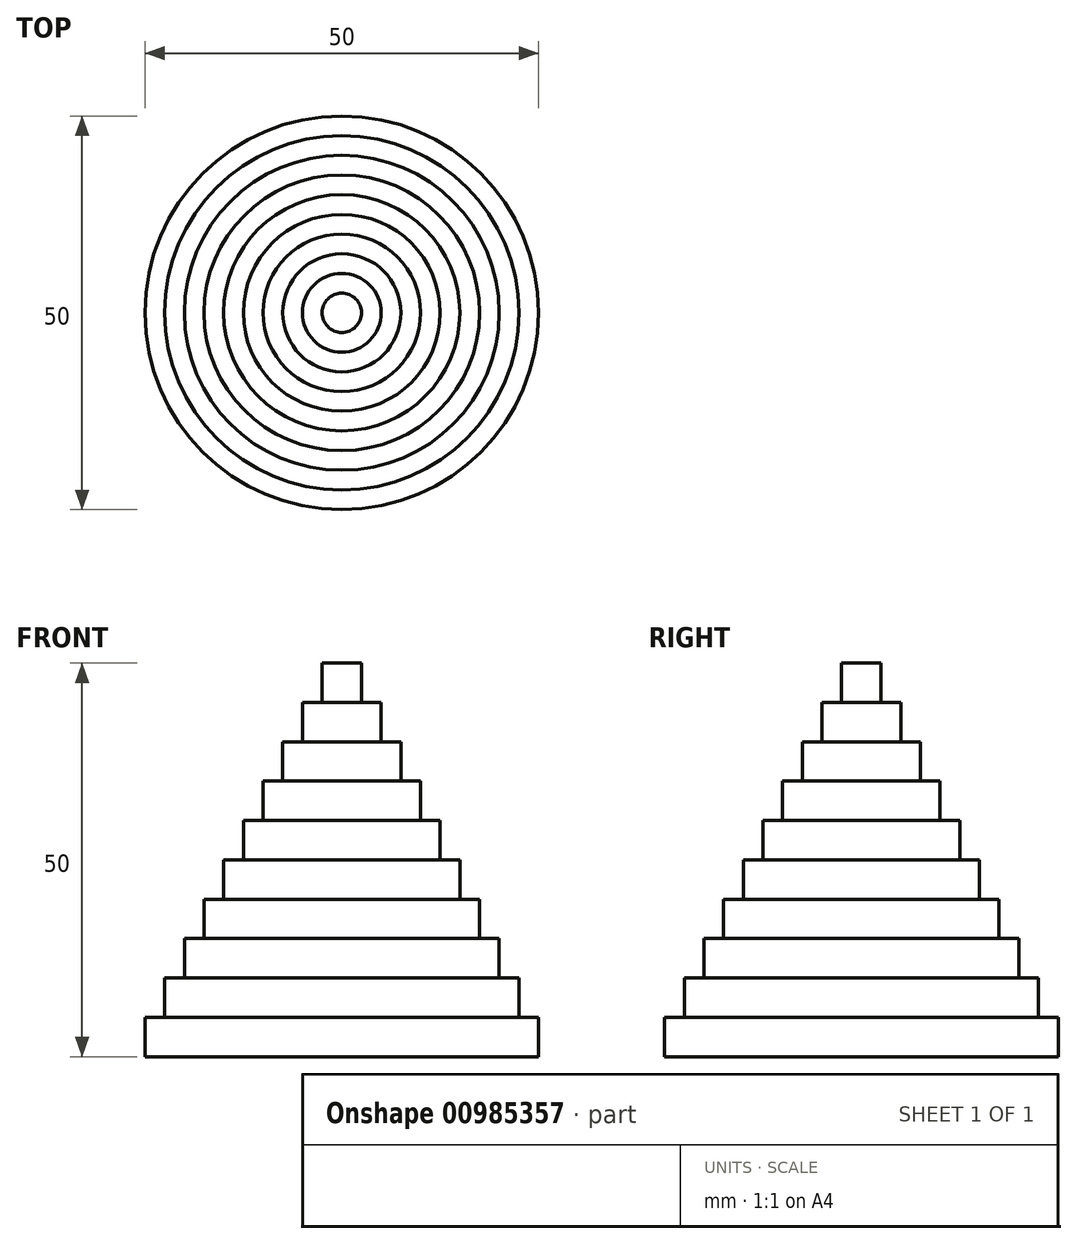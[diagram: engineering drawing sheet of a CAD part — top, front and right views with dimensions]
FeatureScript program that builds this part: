
annotation { "Feature Type Name" : "Feature", "Feature Type Description" : "" }
export const myFeature = defineFeature(function(context is Context, id is Id, definition is map)
    precondition{}
    {
        {
            var Q0;
            Q0=qCreatedBy(makeId("Top.planeOp"),FACE);
            var sketch = newSketch(context, id + "F0", { "sketchPlane" : qUnion([Q0])});
            skCircle(sketch, "E0", {"center": v(0, 0) * mm, "radius": 2.5 * mm});
            skCircle(sketch, "E1", {"center": v(0, 0) * mm, "radius": 5 * mm});
            skCircle(sketch, "E2", {"center": v(0, 0) * mm, "radius": 7.5 * mm});
            skCircle(sketch, "E3", {"center": v(0, 0) * mm, "radius": 10 * mm});
            skCircle(sketch, "E4", {"center": v(0, 0) * mm, "radius": 12.5 * mm});
            skCircle(sketch, "E5", {"center": v(0, 0) * mm, "radius": 15 * mm});
            skCircle(sketch, "E6", {"center": v(0, 0) * mm, "radius": 17.5 * mm});
            skCircle(sketch, "E7", {"center": v(0, 0) * mm, "radius": 20 * mm});
            skCircle(sketch, "E8", {"center": v(0, 0) * mm, "radius": 22.5 * mm});
            skCircle(sketch, "E9", {"center": v(0, 0) * mm, "radius": 25 * mm});
            skSolve(sketch);
        }
        {
            var Q0;
            Q0=makeQuery(id+"F0.imprint","IMPRINT",FACE,{"disambiguationData":[TD([[makeQuery(id+"F0.imprint","IMPRINT",EDGE,{"derivedFrom":sQuery(id+"F0.wireOp",EDGE,"E5")}),-1.0]])]});
            var Q1;
            Q1=makeQuery(id+"F0.imprint","IMPRINT",FACE,{"disambiguationData":[TD([[makeQuery(id+"F0.imprint","IMPRINT",EDGE,{"derivedFrom":sQuery(id+"F0.wireOp",EDGE,"E3")}),-1.0]])]});
            var Q2;
            Q2=makeQuery(id+"F0.imprint","IMPRINT",FACE,{"disambiguationData":[TD([[makeQuery(id+"F0.imprint","IMPRINT",EDGE,{"derivedFrom":sQuery(id+"F0.wireOp",EDGE,"E1")}),-1.0]])]});
            var Q3;
            Q3=makeQuery(id+"F0.imprint","IMPRINT",FACE,{"disambiguationData":[TD([[makeQuery(id+"F0.imprint","IMPRINT",EDGE,{"derivedFrom":sQuery(id+"F0.wireOp",EDGE,"E2")}),-1.0]])]});
            var Q4;
            Q4=makeQuery(id+"F0.imprint","IMPRINT",FACE,{"disambiguationData":[TD([[makeQuery(id+"F0.imprint","IMPRINT",EDGE,{"derivedFrom":sQuery(id+"F0.wireOp",EDGE,"E6")}),-1.0]])]});
            var Q5;
            Q5=makeQuery(id+"F0.imprint","IMPRINT",FACE,{"disambiguationData":[TD([[makeQuery(id+"F0.imprint","IMPRINT",EDGE,{"derivedFrom":sQuery(id+"F0.wireOp",EDGE,"E4")}),-1.0]])]});
            var Q6;
            Q6=makeQuery(id+"F0.imprint","IMPRINT",FACE,{"disambiguationData":[TD([[makeQuery(id+"F0.imprint","IMPRINT",EDGE,{"derivedFrom":sQuery(id+"F0.wireOp",EDGE,"E8")}),-1.0]])]});
            var Q7;
            Q7=makeQuery(id+"F0.imprint","IMPRINT",FACE,{"disambiguationData":[TD([[makeQuery(id+"F0.imprint","IMPRINT",EDGE,{"derivedFrom":sQuery(id+"F0.wireOp",EDGE,"E0")}),1.0]])]});
            var Q8;
            Q8=makeQuery(id+"F0.imprint","IMPRINT",FACE,{"disambiguationData":[TD([[makeQuery(id+"F0.imprint","IMPRINT",EDGE,{"derivedFrom":sQuery(id+"F0.wireOp",EDGE,"E7")}),-1.0]])]});
            var Q9;
            Q9=makeQuery(id+"F0.imprint","IMPRINT",FACE,{"disambiguationData":[TD([[makeQuery(id+"F0.imprint","IMPRINT",EDGE,{"derivedFrom":sQuery(id+"F0.wireOp",EDGE,"E0")}),-1.0]])]});
            extrude(context, id + "F1", {"entities" : qUnion([Q0, Q1, Q2, Q3, Q4, Q5, Q6, Q7, Q8, Q9]), "depth" : 5 * mm, "offsetDistance" : 25 * mm});
        }
        {
            var Q0;
            Q0=makeQuery(id+"F0.imprint","IMPRINT",FACE,{"disambiguationData":[TD([[makeQuery(id+"F0.imprint","IMPRINT",EDGE,{"derivedFrom":sQuery(id+"F0.wireOp",EDGE,"E5")}),-1.0]])]});
            var Q1;
            Q1=makeQuery(id+"F0.imprint","IMPRINT",FACE,{"disambiguationData":[TD([[makeQuery(id+"F0.imprint","IMPRINT",EDGE,{"derivedFrom":sQuery(id+"F0.wireOp",EDGE,"E3")}),-1.0]])]});
            var Q2;
            Q2=makeQuery(id+"F0.imprint","IMPRINT",FACE,{"disambiguationData":[TD([[makeQuery(id+"F0.imprint","IMPRINT",EDGE,{"derivedFrom":sQuery(id+"F0.wireOp",EDGE,"E1")}),-1.0]])]});
            var Q3;
            Q3=makeQuery(id+"F0.imprint","IMPRINT",FACE,{"disambiguationData":[TD([[makeQuery(id+"F0.imprint","IMPRINT",EDGE,{"derivedFrom":sQuery(id+"F0.wireOp",EDGE,"E2")}),-1.0]])]});
            var Q4;
            Q4=makeQuery(id+"F0.imprint","IMPRINT",FACE,{"disambiguationData":[TD([[makeQuery(id+"F0.imprint","IMPRINT",EDGE,{"derivedFrom":sQuery(id+"F0.wireOp",EDGE,"E6")}),-1.0]])]});
            var Q5;
            Q5=makeQuery(id+"F0.imprint","IMPRINT",FACE,{"disambiguationData":[TD([[makeQuery(id+"F0.imprint","IMPRINT",EDGE,{"derivedFrom":sQuery(id+"F0.wireOp",EDGE,"E4")}),-1.0]])]});
            var Q6;
            Q6=makeQuery(id+"F0.imprint","IMPRINT",FACE,{"disambiguationData":[TD([[makeQuery(id+"F0.imprint","IMPRINT",EDGE,{"derivedFrom":sQuery(id+"F0.wireOp",EDGE,"E0")}),1.0]])]});
            var Q7;
            Q7=makeQuery(id+"F0.imprint","IMPRINT",FACE,{"disambiguationData":[TD([[makeQuery(id+"F0.imprint","IMPRINT",EDGE,{"derivedFrom":sQuery(id+"F0.wireOp",EDGE,"E7")}),-1.0]])]});
            var Q8;
            Q8=makeQuery(id+"F0.imprint","IMPRINT",FACE,{"disambiguationData":[TD([[makeQuery(id+"F0.imprint","IMPRINT",EDGE,{"derivedFrom":sQuery(id+"F0.wireOp",EDGE,"E0")}),-1.0]])]});
            extrude(context, id + "F2", {"entities" : qUnion([Q0, Q1, Q2, Q3, Q4, Q5, Q6, Q7, Q8]), "operationType" : NewBodyOperationType.ADD, "depth" : 10 * mm, "offsetDistance" : 25 * mm});
        }
        {
            var Q0;
            Q0=makeQuery(id+"F0.imprint","IMPRINT",FACE,{"disambiguationData":[TD([[makeQuery(id+"F0.imprint","IMPRINT",EDGE,{"derivedFrom":sQuery(id+"F0.wireOp",EDGE,"E5")}),-1.0]])]});
            var Q1;
            Q1=makeQuery(id+"F0.imprint","IMPRINT",FACE,{"disambiguationData":[TD([[makeQuery(id+"F0.imprint","IMPRINT",EDGE,{"derivedFrom":sQuery(id+"F0.wireOp",EDGE,"E3")}),-1.0]])]});
            var Q2;
            Q2=makeQuery(id+"F0.imprint","IMPRINT",FACE,{"disambiguationData":[TD([[makeQuery(id+"F0.imprint","IMPRINT",EDGE,{"derivedFrom":sQuery(id+"F0.wireOp",EDGE,"E1")}),-1.0]])]});
            var Q3;
            Q3=makeQuery(id+"F0.imprint","IMPRINT",FACE,{"disambiguationData":[TD([[makeQuery(id+"F0.imprint","IMPRINT",EDGE,{"derivedFrom":sQuery(id+"F0.wireOp",EDGE,"E2")}),-1.0]])]});
            var Q4;
            Q4=makeQuery(id+"F0.imprint","IMPRINT",FACE,{"disambiguationData":[TD([[makeQuery(id+"F0.imprint","IMPRINT",EDGE,{"derivedFrom":sQuery(id+"F0.wireOp",EDGE,"E6")}),-1.0]])]});
            var Q5;
            Q5=makeQuery(id+"F0.imprint","IMPRINT",FACE,{"disambiguationData":[TD([[makeQuery(id+"F0.imprint","IMPRINT",EDGE,{"derivedFrom":sQuery(id+"F0.wireOp",EDGE,"E4")}),-1.0]])]});
            var Q6;
            Q6=makeQuery(id+"F0.imprint","IMPRINT",FACE,{"disambiguationData":[TD([[makeQuery(id+"F0.imprint","IMPRINT",EDGE,{"derivedFrom":sQuery(id+"F0.wireOp",EDGE,"E0")}),1.0]])]});
            var Q7;
            Q7=makeQuery(id+"F0.imprint","IMPRINT",FACE,{"disambiguationData":[TD([[makeQuery(id+"F0.imprint","IMPRINT",EDGE,{"derivedFrom":sQuery(id+"F0.wireOp",EDGE,"E0")}),-1.0]])]});
            extrude(context, id + "F3", {"entities" : qUnion([Q0, Q1, Q2, Q3, Q4, Q5, Q6, Q7]), "operationType" : NewBodyOperationType.ADD, "depth" : 15 * mm, "offsetDistance" : 25 * mm});
        }
        {
            var Q0;
            Q0=makeQuery(id+"F0.imprint","IMPRINT",FACE,{"disambiguationData":[TD([[makeQuery(id+"F0.imprint","IMPRINT",EDGE,{"derivedFrom":sQuery(id+"F0.wireOp",EDGE,"E0")}),1.0]])]});
            var Q1;
            Q1=makeQuery(id+"F0.imprint","IMPRINT",FACE,{"disambiguationData":[TD([[makeQuery(id+"F0.imprint","IMPRINT",EDGE,{"derivedFrom":sQuery(id+"F0.wireOp",EDGE,"E0")}),-1.0]])]});
            var Q2;
            Q2=makeQuery(id+"F0.imprint","IMPRINT",FACE,{"disambiguationData":[TD([[makeQuery(id+"F0.imprint","IMPRINT",EDGE,{"derivedFrom":sQuery(id+"F0.wireOp",EDGE,"E1")}),-1.0]])]});
            var Q3;
            Q3=makeQuery(id+"F0.imprint","IMPRINT",FACE,{"disambiguationData":[TD([[makeQuery(id+"F0.imprint","IMPRINT",EDGE,{"derivedFrom":sQuery(id+"F0.wireOp",EDGE,"E2")}),-1.0]])]});
            var Q4;
            Q4=makeQuery(id+"F0.imprint","IMPRINT",FACE,{"disambiguationData":[TD([[makeQuery(id+"F0.imprint","IMPRINT",EDGE,{"derivedFrom":sQuery(id+"F0.wireOp",EDGE,"E3")}),-1.0]])]});
            var Q5;
            Q5=makeQuery(id+"F0.imprint","IMPRINT",FACE,{"disambiguationData":[TD([[makeQuery(id+"F0.imprint","IMPRINT",EDGE,{"derivedFrom":sQuery(id+"F0.wireOp",EDGE,"E4")}),-1.0]])]});
            var Q6;
            Q6=makeQuery(id+"F0.imprint","IMPRINT",FACE,{"disambiguationData":[TD([[makeQuery(id+"F0.imprint","IMPRINT",EDGE,{"derivedFrom":sQuery(id+"F0.wireOp",EDGE,"E5")}),-1.0]])]});
            extrude(context, id + "F4", {"entities" : qUnion([Q0, Q1, Q2, Q3, Q4, Q5, Q6]), "operationType" : NewBodyOperationType.ADD, "depth" : 20 * mm, "offsetDistance" : 25 * mm});
        }
        {
            var Q0;
            Q0=makeQuery(id+"F0.imprint","IMPRINT",FACE,{"disambiguationData":[TD([[makeQuery(id+"F0.imprint","IMPRINT",EDGE,{"derivedFrom":sQuery(id+"F0.wireOp",EDGE,"E0")}),1.0]])]});
            var Q1;
            Q1=makeQuery(id+"F0.imprint","IMPRINT",FACE,{"disambiguationData":[TD([[makeQuery(id+"F0.imprint","IMPRINT",EDGE,{"derivedFrom":sQuery(id+"F0.wireOp",EDGE,"E0")}),-1.0]])]});
            var Q2;
            Q2=makeQuery(id+"F0.imprint","IMPRINT",FACE,{"disambiguationData":[TD([[makeQuery(id+"F0.imprint","IMPRINT",EDGE,{"derivedFrom":sQuery(id+"F0.wireOp",EDGE,"E1")}),-1.0]])]});
            var Q3;
            Q3=makeQuery(id+"F0.imprint","IMPRINT",FACE,{"disambiguationData":[TD([[makeQuery(id+"F0.imprint","IMPRINT",EDGE,{"derivedFrom":sQuery(id+"F0.wireOp",EDGE,"E2")}),-1.0]])]});
            var Q4;
            Q4=makeQuery(id+"F0.imprint","IMPRINT",FACE,{"disambiguationData":[TD([[makeQuery(id+"F0.imprint","IMPRINT",EDGE,{"derivedFrom":sQuery(id+"F0.wireOp",EDGE,"E3")}),-1.0]])]});
            var Q5;
            Q5=makeQuery(id+"F0.imprint","IMPRINT",FACE,{"disambiguationData":[TD([[makeQuery(id+"F0.imprint","IMPRINT",EDGE,{"derivedFrom":sQuery(id+"F0.wireOp",EDGE,"E4")}),-1.0]])]});
            extrude(context, id + "F5", {"entities" : qUnion([Q0, Q1, Q2, Q3, Q4, Q5]), "operationType" : NewBodyOperationType.ADD, "depth" : 25 * mm, "offsetDistance" : 25 * mm});
        }
        {
            var Q0;
            Q0=makeQuery(id+"F0.imprint","IMPRINT",FACE,{"disambiguationData":[TD([[makeQuery(id+"F0.imprint","IMPRINT",EDGE,{"derivedFrom":sQuery(id+"F0.wireOp",EDGE,"E0")}),1.0]])]});
            var Q1;
            Q1=makeQuery(id+"F0.imprint","IMPRINT",FACE,{"disambiguationData":[TD([[makeQuery(id+"F0.imprint","IMPRINT",EDGE,{"derivedFrom":sQuery(id+"F0.wireOp",EDGE,"E0")}),-1.0]])]});
            var Q2;
            Q2=makeQuery(id+"F0.imprint","IMPRINT",FACE,{"disambiguationData":[TD([[makeQuery(id+"F0.imprint","IMPRINT",EDGE,{"derivedFrom":sQuery(id+"F0.wireOp",EDGE,"E1")}),-1.0]])]});
            var Q3;
            Q3=makeQuery(id+"F0.imprint","IMPRINT",FACE,{"disambiguationData":[TD([[makeQuery(id+"F0.imprint","IMPRINT",EDGE,{"derivedFrom":sQuery(id+"F0.wireOp",EDGE,"E2")}),-1.0]])]});
            var Q4;
            Q4=makeQuery(id+"F0.imprint","IMPRINT",FACE,{"disambiguationData":[TD([[makeQuery(id+"F0.imprint","IMPRINT",EDGE,{"derivedFrom":sQuery(id+"F0.wireOp",EDGE,"E3")}),-1.0]])]});
            extrude(context, id + "F6", {"entities" : qUnion([Q0, Q1, Q2, Q3, Q4]), "operationType" : NewBodyOperationType.ADD, "depth" : 30 * mm, "offsetDistance" : 25 * mm});
        }
        {
            var Q0;
            Q0=makeQuery(id+"F0.imprint","IMPRINT",FACE,{"disambiguationData":[TD([[makeQuery(id+"F0.imprint","IMPRINT",EDGE,{"derivedFrom":sQuery(id+"F0.wireOp",EDGE,"E2")}),-1.0]])]});
            var Q1;
            Q1=makeQuery(id+"F0.imprint","IMPRINT",FACE,{"disambiguationData":[TD([[makeQuery(id+"F0.imprint","IMPRINT",EDGE,{"derivedFrom":sQuery(id+"F0.wireOp",EDGE,"E1")}),-1.0]])]});
            var Q2;
            Q2=makeQuery(id+"F0.imprint","IMPRINT",FACE,{"disambiguationData":[TD([[makeQuery(id+"F0.imprint","IMPRINT",EDGE,{"derivedFrom":sQuery(id+"F0.wireOp",EDGE,"E0")}),-1.0]])]});
            var Q3;
            Q3=makeQuery(id+"F0.imprint","IMPRINT",FACE,{"disambiguationData":[TD([[makeQuery(id+"F0.imprint","IMPRINT",EDGE,{"derivedFrom":sQuery(id+"F0.wireOp",EDGE,"E0")}),1.0]])]});
            extrude(context, id + "F7", {"entities" : qUnion([Q0, Q1, Q2, Q3]), "operationType" : NewBodyOperationType.ADD, "depth" : 35 * mm, "offsetDistance" : 25 * mm});
        }
        {
            var Q0;
            Q0=makeQuery(id+"F0.imprint","IMPRINT",FACE,{"disambiguationData":[TD([[makeQuery(id+"F0.imprint","IMPRINT",EDGE,{"derivedFrom":sQuery(id+"F0.wireOp",EDGE,"E0")}),1.0]])]});
            var Q1;
            Q1=makeQuery(id+"F0.imprint","IMPRINT",FACE,{"disambiguationData":[TD([[makeQuery(id+"F0.imprint","IMPRINT",EDGE,{"derivedFrom":sQuery(id+"F0.wireOp",EDGE,"E0")}),-1.0]])]});
            var Q2;
            Q2=makeQuery(id+"F0.imprint","IMPRINT",FACE,{"disambiguationData":[TD([[makeQuery(id+"F0.imprint","IMPRINT",EDGE,{"derivedFrom":sQuery(id+"F0.wireOp",EDGE,"E1")}),-1.0]])]});
            extrude(context, id + "F8", {"entities" : qUnion([Q0, Q1, Q2]), "operationType" : NewBodyOperationType.ADD, "depth" : 40 * mm, "offsetDistance" : 25 * mm});
        }
        {
            var Q0;
            Q0=makeQuery(id+"F0.imprint","IMPRINT",FACE,{"disambiguationData":[TD([[makeQuery(id+"F0.imprint","IMPRINT",EDGE,{"derivedFrom":sQuery(id+"F0.wireOp",EDGE,"E0")}),-1.0]])]});
            var Q1;
            Q1=makeQuery(id+"F0.imprint","IMPRINT",FACE,{"disambiguationData":[TD([[makeQuery(id+"F0.imprint","IMPRINT",EDGE,{"derivedFrom":sQuery(id+"F0.wireOp",EDGE,"E0")}),1.0]])]});
            extrude(context, id + "F9", {"entities" : qUnion([Q0, Q1]), "operationType" : NewBodyOperationType.ADD, "depth" : 45 * mm, "offsetDistance" : 25 * mm});
        }
        {
            var Q0;
            Q0=makeQuery(id+"F0.imprint","IMPRINT",FACE,{"disambiguationData":[TD([[makeQuery(id+"F0.imprint","IMPRINT",EDGE,{"derivedFrom":sQuery(id+"F0.wireOp",EDGE,"E0")}),1.0]])]});
            extrude(context, id + "F10", {"entities" : qUnion([Q0]), "operationType" : NewBodyOperationType.ADD, "depth" : 50 * mm, "offsetDistance" : 25 * mm});
        }
    });
